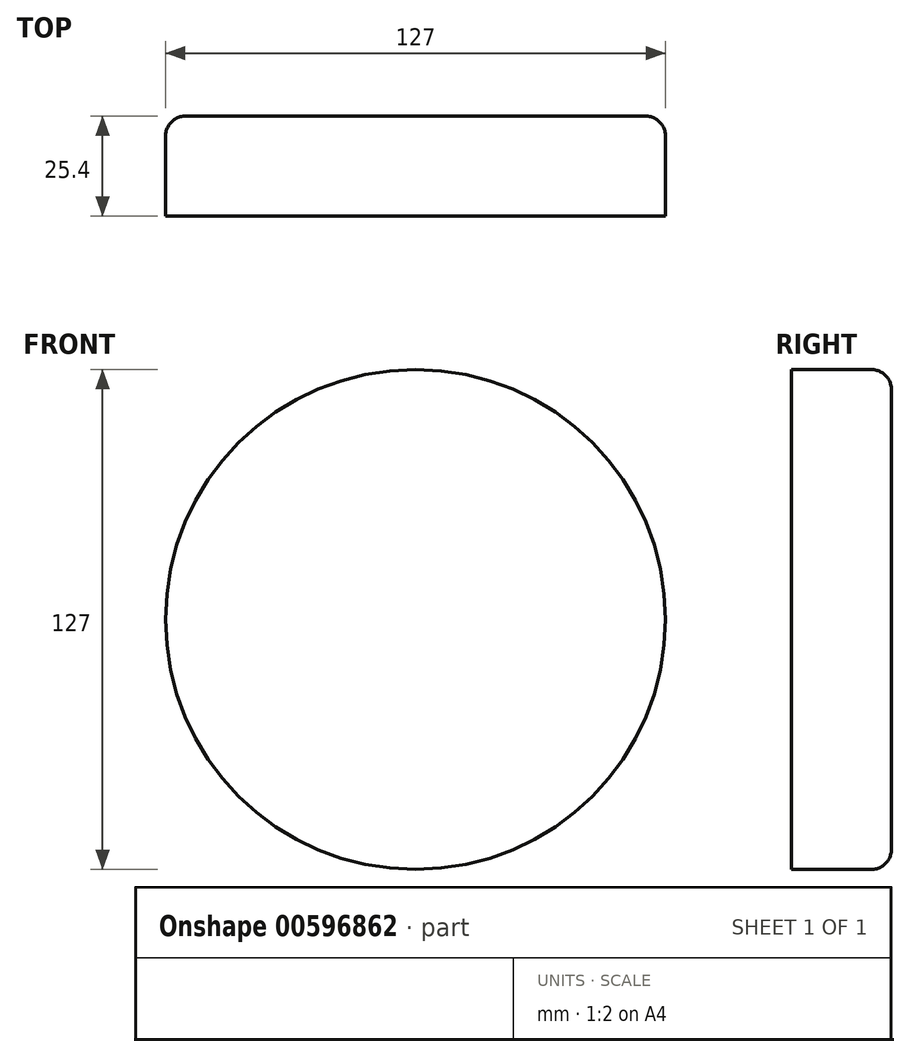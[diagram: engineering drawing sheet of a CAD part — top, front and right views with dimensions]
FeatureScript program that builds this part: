
annotation { "Feature Type Name" : "Feature", "Feature Type Description" : "" }
export const myFeature = defineFeature(function(context is Context, id is Id, definition is map)
    precondition{}
    {
        {
            var Q0;
            Q0=qCreatedBy(makeId("Front.planeOp"),FACE);
            var sketch = newSketch(context, id + "F0", { "sketchPlane" : qUnion([Q0])});
            skCircle(sketch, "E0", {"center": v(0, 0) * mm, "radius": 63.5 * mm});
            skSolve(sketch);
        }
        {
            var Q0;
            Q0=makeQuery(id+"F0.imprint","IMPRINT",FACE,{"disambiguationData":[TD([[makeQuery(id+"F0.imprint","IMPRINT",EDGE,{"derivedFrom":sQuery(id+"F0.wireOp",EDGE,"E0")}),1.0]])]});
            extrude(context, id + "F1", {"entities" : qUnion([Q0]), "depth" : 25.4 * mm, "offsetDistance" : 25.4 * mm});
        }
        {
            var Q0;
            Q0=qCreatedBy(makeId("Front.planeOp"),FACE);
            var sketch = newSketch(context, id + "F2", { "sketchPlane" : qUnion([Q0])});
            skCircle(sketch, "E1", {"center": v(0, 0) * mm, "radius": 6.35 * mm});
            skSolve(sketch);
        }
        {
            var Q0;
            Q0=sQuery(id+"F2.wireOp",EDGE,"E1");
            extrude(context, id + "F3", {"bodyType" : ToolBodyType.SURFACE, "surfaceEntities" : qUnion([Q0]), "endBound" : BoundingType.THROUGH_ALL, "oppositeDirection" : true, "depth" : 25.4 * mm, "offsetDistance" : 25.4 * mm});
        }
        {
            var Q0;
            Q0=makeQuery(id+"F1.opExtrude","CAP_EDGE",EDGE,{"disambiguationData":[OSD([sQuery(id+"F0.wireOp",EDGE,"E0")])],"isStart":true});
            fillet(context, id + "F4", {"entities" : qUnion([Q0]), "radius" : 5.08 * mm, "tangentPropagation" : true, "allowEdgeOverflow" : false});
        }
    });
